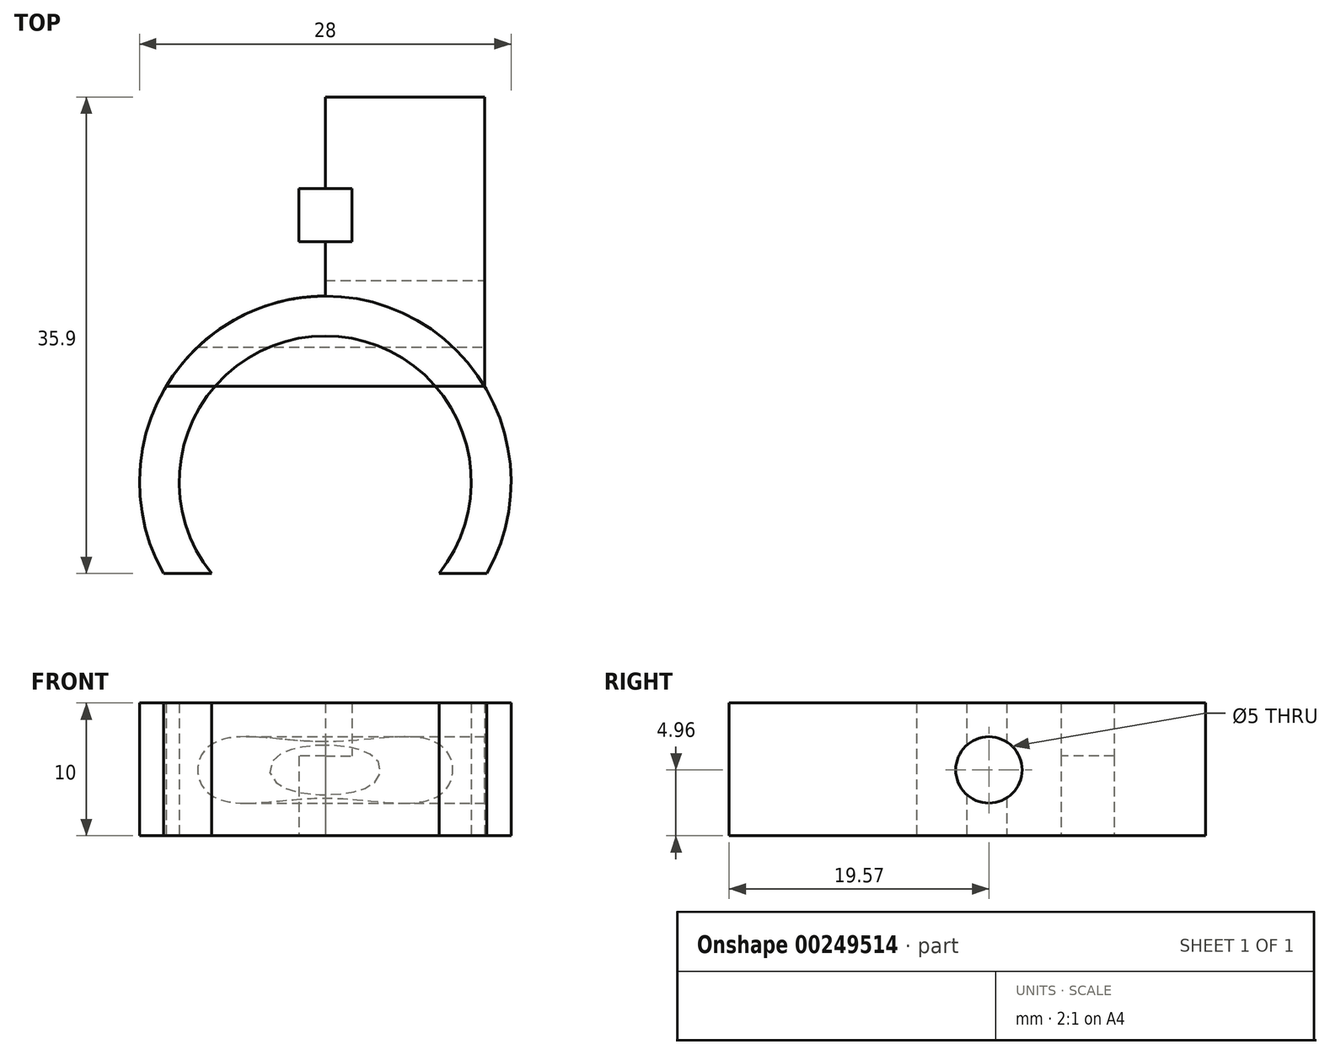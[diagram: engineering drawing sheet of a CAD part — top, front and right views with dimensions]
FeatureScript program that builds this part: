
annotation { "Feature Type Name" : "Feature", "Feature Type Description" : "" }
export const myFeature = defineFeature(function(context is Context, id is Id, definition is map)
    precondition{}
    {
        {
            var Q0;
            Q0=qCreatedBy(makeId("Top.planeOp"),FACE);
            var sketch = newSketch(context, id + "F0", { "sketchPlane" : qUnion([Q0])});
            skCircle(sketch, "E0", {"center": v(0, 0) * mm, "radius": 14 * mm});
            skLineSegment(sketch, "E1.bottom", {"start": v(-18.2, -6.9) * mm, "end": v(15.98, -6.9) * mm});
            skLineSegment(sketch, "E1.top", {"start": v(-18.2, -17.65) * mm, "end": v(15.98, -17.65) * mm});
            skLineSegment(sketch, "E1.left", {"start": v(-18.2, -6.9) * mm, "end": v(-18.2, -17.65) * mm});
            skLineSegment(sketch, "E1.right", {"start": v(15.98, -6.9) * mm, "end": v(15.98, -17.65) * mm});
            skPoint(sketch, "E2.middle", {"position": v(0, 14) * mm});
            skLineSegment(sketch, "E3", {"start": v(0, 14) * mm, "end": v(0, 29) * mm});
            skLineSegment(sketch, "E4", {"start": v(0, 29) * mm, "end": v(12, 29) * mm});
            skLineSegment(sketch, "E5", {"start": v(12, 29) * mm, "end": v(12, 7.21) * mm});
            skLineSegment(sketch, "E6", {"start": v(12, 7.21) * mm, "end": v(-12, 7.21) * mm});
            skLineSegment(sketch, "E7", {"start": v(0, 29) * mm, "end": v(-12, 29) * mm});
            skLineSegment(sketch, "E8", {"start": v(-12, 7.21) * mm, "end": v(-12, 29) * mm});
            skLineSegment(sketch, "E9", {"start": v(0, 29) * mm, "end": v(0, 22.1) * mm});
            skLineSegment(sketch, "E10", {"start": v(0, 22.1) * mm, "end": v(2, 22.1) * mm});
            skLineSegment(sketch, "E11", {"start": v(2, 22.1) * mm, "end": v(2, 18.1) * mm});
            skLineSegment(sketch, "E12", {"start": v(2, 18.1) * mm, "end": v(-2, 18.1) * mm});
            skLineSegment(sketch, "E13", {"start": v(-2, 18.1) * mm, "end": v(-2, 22.1) * mm});
            skLineSegment(sketch, "E14", {"start": v(-2, 22.1) * mm, "end": v(0, 22.1) * mm});
            skSolve(sketch);
        }
        {
            var Q0;
            {var subQ0=sQuery(id+"F0.wireOp",EDGE,"E1.bottom");var subQ1=sQuery(id+"F0.wireOp",EDGE,"E0");var subQ2=makeQuery(id+"F0.imprint","INTERSECT",VERTEX,{"disambiguationData":[OD(0.0)],"derivedFrom":[subQ1,subQ0]});Q0=makeQuery(id+"F0.imprint","IMPRINT",FACE,{"disambiguationData":[TD([[makeQuery(id+"F0.imprint","IMPRINT",EDGE,{"disambiguationData":[TD([[subQ2,1.0]])],"derivedFrom":subQ1}),1.0]])]});}
            var Q1;
            {var subQ0=sQuery(id+"F0.wireOp",EDGE,"E1.bottom");var subQ1=sQuery(id+"F0.wireOp",EDGE,"E0");var subQ2=makeQuery(id+"F0.imprint","INTERSECT",VERTEX,{"disambiguationData":[OD(0.0)],"derivedFrom":[subQ1,subQ0]});Q1=makeQuery(id+"F0.imprint","IMPRINT",FACE,{"disambiguationData":[TD([[makeQuery(id+"F0.imprint","IMPRINT",EDGE,{"disambiguationData":[TD([[subQ2,-1.0]])],"derivedFrom":subQ1}),1.0]])]});}
            var Q2;
            {var subQ0=sQuery(id+"F0.wireOp",EDGE,"E2.top");var subQ1=sQuery(id+"F0.wireOp",EDGE,"E0");var subQ2=makeQuery(id+"F0.imprint","INTERSECT",VERTEX,{"disambiguationData":[OD(0.0)],"derivedFrom":[subQ1,subQ0]});Q2=makeQuery(id+"F0.imprint","IMPRINT",FACE,{"disambiguationData":[TD([[makeQuery(id+"F0.imprint","IMPRINT",EDGE,{"disambiguationData":[TD([[subQ2,1.0]])],"derivedFrom":subQ1}),1.0]])]});}
            var Q3;
            {var subQ2=sQuery(id+"F0.wireOp",EDGE,"E6");Q3=makeQuery(id+"F0.imprint","IMPRINT",FACE,{"disambiguationData":[TD([[makeQuery(id+"F0.imprint","IMPRINT",EDGE,{"derivedFrom":subQ2}),-1.0]])]});}
            var Q4;
            {var subQ0=sQuery(id+"F0.wireOp",EDGE,"wFob2Agy-zdrX-jafj-vTLI-2I8QICY1NMm5");Q4=makeQuery(id+"F0.imprint","IMPRINT",FACE,{"disambiguationData":[TD([[makeQuery(id+"F0.imprint","IMPRINT",EDGE,{"derivedFrom":subQ0}),-1.0]])]});}
            var Q5;
            {var subQ0=sQuery(id+"F0.wireOp",EDGE,"x5XBvrcF-CRTP-LSSV-CU9F-8jN8pTNf4zUS");Q5=makeQuery(id+"F0.imprint","IMPRINT",FACE,{"disambiguationData":[TD([[makeQuery(id+"F0.imprint","IMPRINT",EDGE,{"derivedFrom":subQ0}),-1.0]])]});}
            var Q6;
            {var subQ5=sQuery(id+"F0.wireOp",EDGE,"pjZ81xTJ-YRqA-lnuf-JboY-ewq08NkR8L1C");Q6=makeQuery(id+"F0.imprint","IMPRINT",FACE,{"disambiguationData":[TD([[makeQuery(id+"F0.imprint","IMPRINT",EDGE,{"derivedFrom":subQ5}),-1.0]])]});}
            extrude(context, id + "F1", {"entities" : qUnion([Q0, Q1, Q2, Q3, Q4, Q5, Q6]), "depth" : 10 * mm, "flatOperationType" : FlatOperationType.REMOVE, "offsetDistance" : 25 * mm, "domain" : OperationDomain.MODEL});
        }
        {
            var Q0;
            {var subQ0=sQuery(id+"F0.wireOp",EDGE,"E8");Q0=makeQuery(id+"F0.imprint","IMPRINT",FACE,{"disambiguationData":[TD([[makeQuery(id+"F0.imprint","IMPRINT",EDGE,{"derivedFrom":subQ0}),-1.0]])]});}
            var Q1;
            Q1=makeQuery(id+"F0.imprint","IMPRINT",FACE,{"disambiguationData":[TD([[makeQuery(id+"F0.imprint","IMPRINT",EDGE,{"derivedFrom":sQuery(id+"F0.wireOp",EDGE,"E4")}),-1.0]])]});
            extrude(context, id + "F2", {"entities" : qUnion([Q0, Q1]), "flatOperationType" : FlatOperationType.REMOVE, "depth" : 10 * mm, "offsetDistance" : 25 * mm, "domain" : OperationDomain.MODEL});
        }
        {
            var Q0;
            Q0=makeQuery(id+"F1.opExtrude","CAP_FACE",FACE,{"disambiguationData":[OSD([sQuery(id+"F0.wireOp",EDGE,"E0")])],"isStart":true});
            var Q1;
            Q1=makeQuery(id+"F1.opExtrude","CAP_FACE",FACE,{"disambiguationData":[OSD([sQuery(id+"F0.wireOp",EDGE,"E0")])],"isStart":false});
            shell(context, id + "F3", {"entities" : qUnion([Q0, Q1]), "thickness" : 3 * mm});
        }
        {
            var Q0;
            Q0=makeQuery(id+"F0.imprint","IMPRINT",FACE,{"disambiguationData":[TD([[makeQuery(id+"F0.imprint","IMPRINT",EDGE,{"derivedFrom":sQuery(id+"F0.wireOp",EDGE,"E1.top")}),1.0]])]});
            var Q1;
            {var subQ0=sQuery(id+"F0.wireOp",EDGE,"E1.bottom");var subQ1=sQuery(id+"F0.wireOp",EDGE,"E0");var subQ2=makeQuery(id+"F0.imprint","INTERSECT",VERTEX,{"disambiguationData":[OD(0.0)],"derivedFrom":[subQ1,subQ0]});Q1=makeQuery(id+"F0.imprint","IMPRINT",FACE,{"disambiguationData":[TD([[makeQuery(id+"F0.imprint","IMPRINT",EDGE,{"disambiguationData":[TD([[subQ2,-1.0]])],"derivedFrom":subQ1}),1.0]])]});}
            extrude(context, id + "F4", {"entities" : qUnion([Q0, Q1]), "operationType" : NewBodyOperationType.REMOVE, "flatOperationType" : FlatOperationType.REMOVE, "offsetDistance" : 25 * mm, "depth" : 10 * mm, "domain" : OperationDomain.MODEL});
        }
        {
            var Q0;
            Q0=qCreatedBy(makeId("Right.planeOp"),FACE);
            var sketch = newSketch(context, id + "F5", { "sketchPlane" : qUnion([Q0])});
            skLineSegment(sketch, "E15", {"start": v(7.26, 0) * mm, "end": v(28.96, 9.9) * mm});
            skLineSegment(sketch, "E16", {"start": v(29.03, 0) * mm, "end": v(7.2, 9.96) * mm});
            skLineSegment(sketch, "E17", {"start": v(18.15, 4.96) * mm, "end": v(7.2, 4.96) * mm});
            skPoint(sketch, "E18", {"position": v(12.67, 4.96) * mm});
            skCircle(sketch, "E19", {"center": v(12.67, 4.96) * mm, "radius": 2.5 * mm});
            skSolve(sketch);
        }
        {
            var Q0;
            {var subQ0=sQuery(id+"F5.wireOp",EDGE,"E19");var subQ1=sQuery(id+"F5.wireOp",EDGE,"E16");var subQ2=makeQuery(id+"F5.imprint","INTERSECT",VERTEX,{"disambiguationData":[OD(0.0)],"derivedFrom":[subQ1,subQ0]});Q0=makeQuery(id+"F5.imprint","IMPRINT",FACE,{"disambiguationData":[TD([[makeQuery(id+"F5.imprint","IMPRINT",EDGE,{"disambiguationData":[TD([[subQ2,1.0]])],"derivedFrom":subQ1}),-1.0]])]});}
            var Q1;
            {var subQ0=sQuery(id+"F5.wireOp",EDGE,"E19");var subQ1=sQuery(id+"F5.wireOp",EDGE,"E16");var subQ2=makeQuery(id+"F5.imprint","INTERSECT",VERTEX,{"disambiguationData":[OD(0.0)],"derivedFrom":[subQ1,subQ0]});Q1=makeQuery(id+"F5.imprint","IMPRINT",FACE,{"disambiguationData":[TD([[makeQuery(id+"F5.imprint","IMPRINT",EDGE,{"disambiguationData":[TD([[subQ2,1.0]])],"derivedFrom":subQ1}),1.0]])]});}
            var Q2;
            {var subQ0=sQuery(id+"F5.wireOp",EDGE,"E19");var subQ1=sQuery(id+"F5.wireOp",EDGE,"E15");var subQ2=makeQuery(id+"F5.imprint","INTERSECT",VERTEX,{"disambiguationData":[OD(0.0)],"derivedFrom":[subQ1,subQ0]});Q2=makeQuery(id+"F5.imprint","IMPRINT",FACE,{"disambiguationData":[TD([[makeQuery(id+"F5.imprint","IMPRINT",EDGE,{"disambiguationData":[TD([[subQ2,-1.0]])],"derivedFrom":subQ1}),1.0]])]});}
            var Q3;
            {var subQ0=sQuery(id+"F5.wireOp",EDGE,"E19");var subQ1=sQuery(id+"F5.wireOp",EDGE,"E15");var subQ2=makeQuery(id+"F5.imprint","INTERSECT",VERTEX,{"disambiguationData":[OD(0.0)],"derivedFrom":[subQ1,subQ0]});Q3=makeQuery(id+"F5.imprint","IMPRINT",FACE,{"disambiguationData":[TD([[makeQuery(id+"F5.imprint","IMPRINT",EDGE,{"disambiguationData":[TD([[subQ2,-1.0]])],"derivedFrom":subQ1}),-1.0]])]});}
            extrude(context, id + "F6", {"entities" : qUnion([Q0, Q1, Q2, Q3]), "operationType" : NewBodyOperationType.REMOVE, "oppositeDirection" : true, "depth" : 25 * mm, "hasSecondDirection" : true, "secondDirectionOppositeDirection" : false, "secondDirectionDepth" : 25 * mm, "offsetDistance" : 25 * mm});
        }
        {
            var Q0;
            {var subQ0=sQuery(id+"F0.wireOp",EDGE,"E10");Q0=makeQuery(id+"F0.imprint","IMPRINT",FACE,{"disambiguationData":[TD([[makeQuery(id+"F0.imprint","IMPRINT",EDGE,{"derivedFrom":subQ0}),-1.0]])]});}
            var Q1;
            {var subQ4=sQuery(id+"F0.wireOp",EDGE,"E13");Q1=makeQuery(id+"F0.imprint","IMPRINT",FACE,{"disambiguationData":[TD([[makeQuery(id+"F0.imprint","IMPRINT",EDGE,{"derivedFrom":subQ4}),-1.0]])]});}
            extrude(context, id + "F7", {"entities" : qUnion([Q0, Q1]), "operationType" : NewBodyOperationType.ADD, "flatOperationType" : FlatOperationType.REMOVE, "depth" : 6 * mm, "offsetDistance" : 25 * mm, "domain" : OperationDomain.MODEL});
        }
    });
